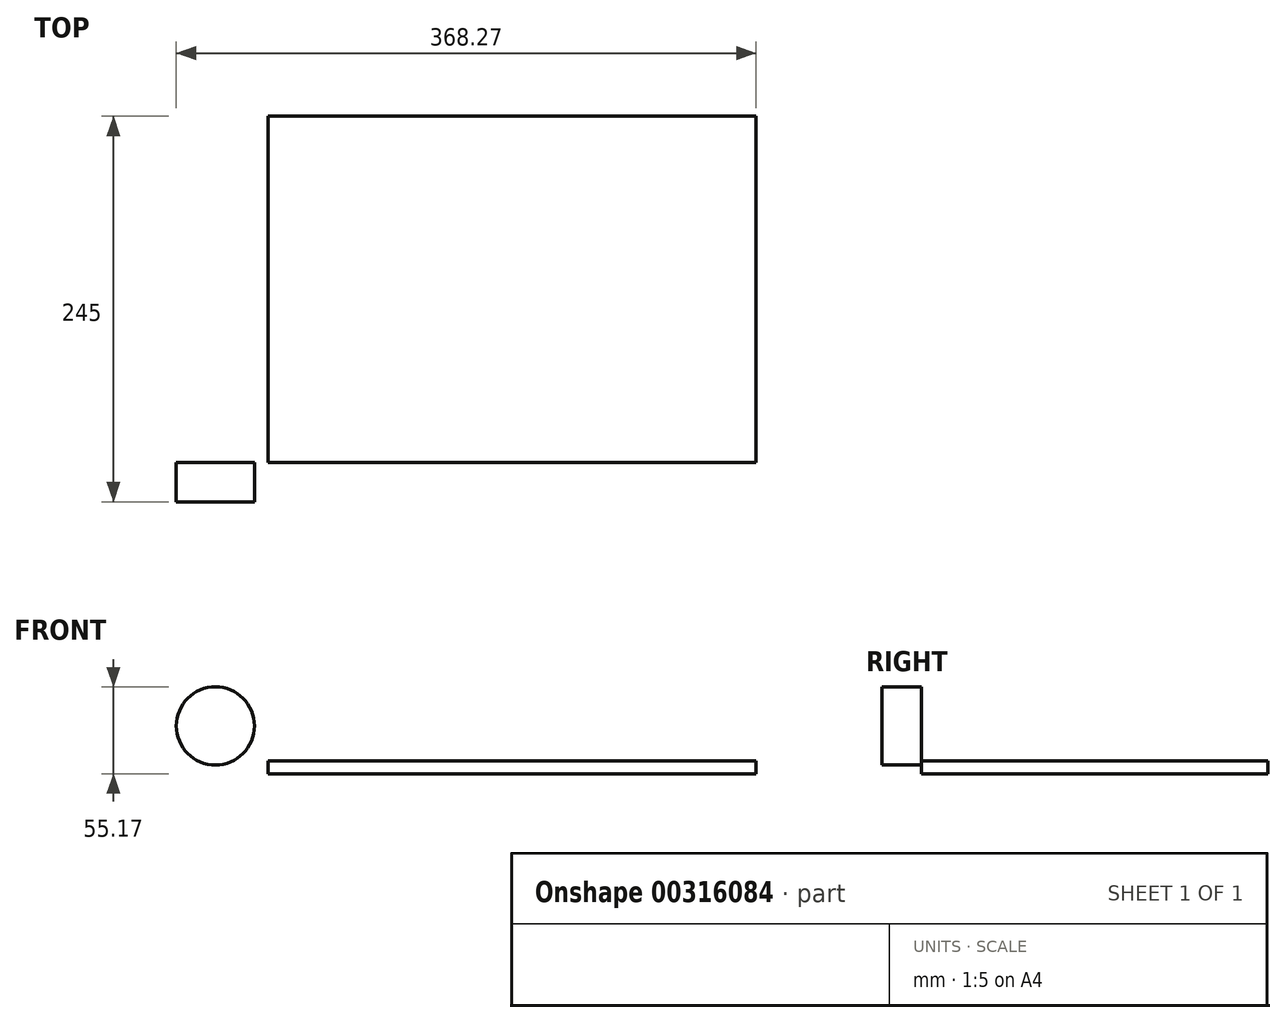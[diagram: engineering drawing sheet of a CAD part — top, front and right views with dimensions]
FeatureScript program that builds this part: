
annotation { "Feature Type Name" : "Feature", "Feature Type Description" : "" }
export const myFeature = defineFeature(function(context is Context, id is Id, definition is map)
    precondition{}
    {
        {
            var Q0;
            Q0=qCreatedBy(makeId("Top.planeOp"),FACE);
            var sketch = newSketch(context, id + "F0", { "sketchPlane" : qUnion([Q0])});
            skLineSegment(sketch, "E0.bottom", {"start": v(0, 0) * mm, "end": v(310, 0) * mm});
            skLineSegment(sketch, "E0.top", {"start": v(0, 220) * mm, "end": v(310, 220) * mm});
            skLineSegment(sketch, "E0.left", {"start": v(0, 0) * mm, "end": v(0, 220) * mm});
            skLineSegment(sketch, "E0.right", {"start": v(310, 0) * mm, "end": v(310, 220) * mm});
            skSolve(sketch);
        }
        {
            var Q0;
            Q0=makeQuery(id+"F0.imprint","IMPRINT",FACE,{"disambiguationData":[TD([[makeQuery(id+"F0.imprint","IMPRINT",EDGE,{"derivedFrom":sQuery(id+"F0.wireOp",EDGE,"E0.bottom")}),1.0]])]});
            extrude(context, id + "F1", {"entities" : qUnion([Q0]), "depth" : 8 * mm});
        }
        {
            var Q0;
            Q0=qCreatedBy(makeId("Front.planeOp"),FACE);
            var sketch = newSketch(context, id + "F2", { "sketchPlane" : qUnion([Q0])});
            skCircle(sketch, "E1", {"center": v(-33.45, 30.35) * mm, "radius": 24.82 * mm});
            skSolve(sketch);
        }
        {
            var Q0;
            Q0=makeQuery(id+"F2.imprint","IMPRINT",FACE,{"disambiguationData":[TD([[makeQuery(id+"F2.imprint","IMPRINT",EDGE,{"derivedFrom":sQuery(id+"F2.wireOp",EDGE,"E1")}),1.0]])]});
            var Q1;
            Q1 = qConstructionFilter(qBodyType(qCreatedBy(id + "F2" ,EDGE), BodyType.WIRE), ConstructionObject.NO);
            extrude(context, id + "F3", {"entities" : qUnion([Q0]), "surfaceEntities" : qUnion([Q1]), "depth" : 25 * mm});
        }
    });
